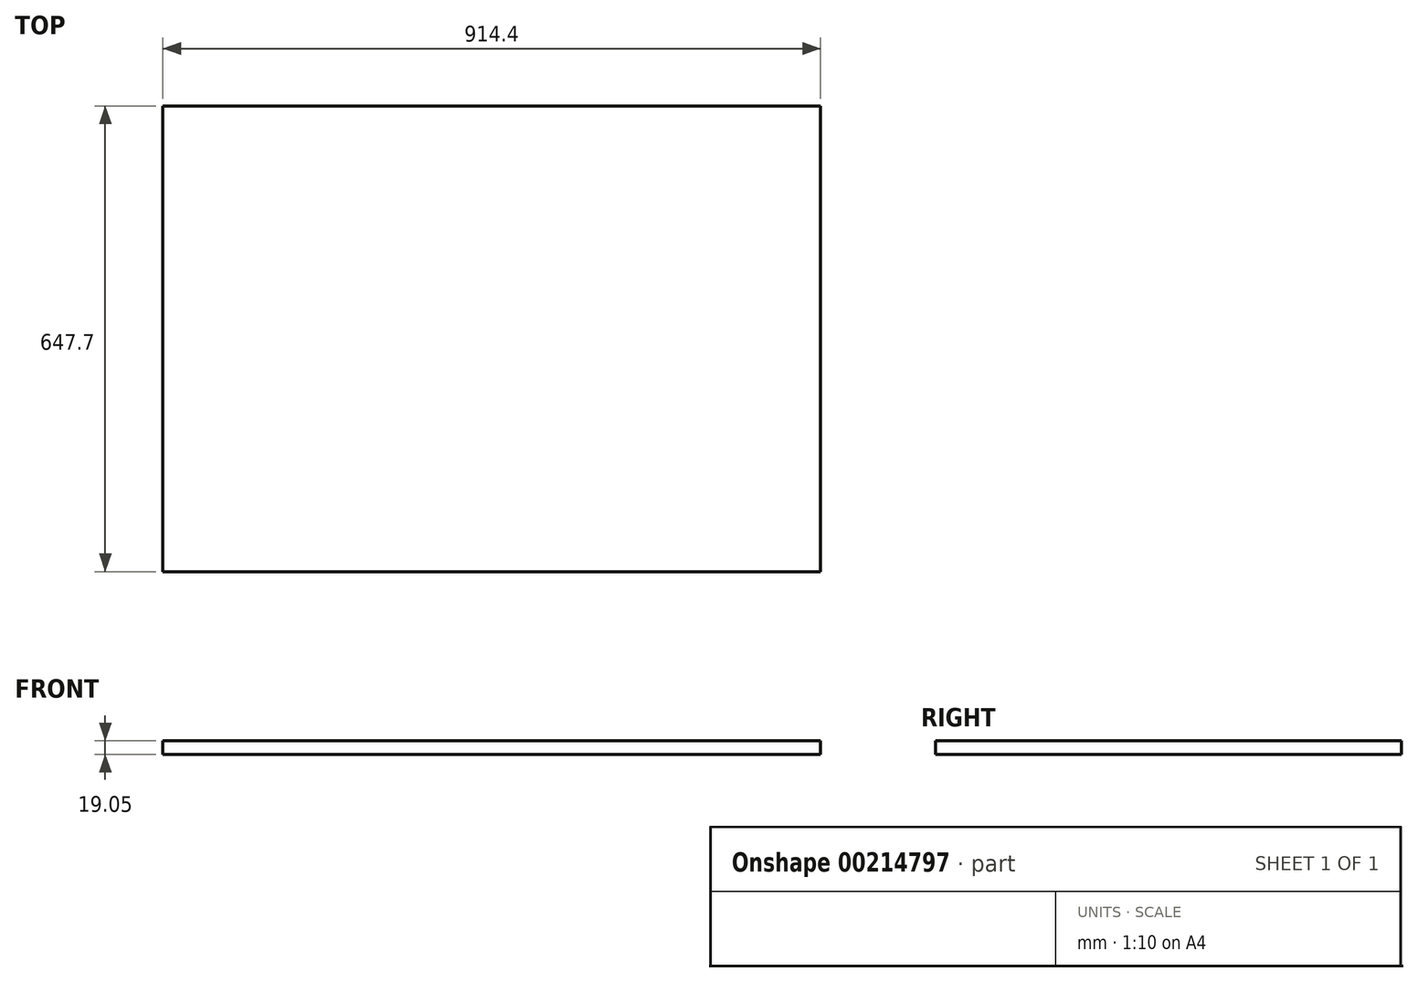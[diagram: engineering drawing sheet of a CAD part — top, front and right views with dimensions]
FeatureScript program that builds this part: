
annotation { "Feature Type Name" : "Feature", "Feature Type Description" : "" }
export const myFeature = defineFeature(function(context is Context, id is Id, definition is map)
    precondition{}
    {
        {
            var Q0;
            Q0=qCreatedBy(makeId("Top.planeOp"),FACE);
            var sketch = newSketch(context, id + "F0", { "sketchPlane" : qUnion([Q0])});
            skLineSegment(sketch, "E0.bottom", {"start": v(0, 0) * mm, "end": v(914.4, 0) * mm});
            skLineSegment(sketch, "E0.top", {"start": v(0, -647.7) * mm, "end": v(914.4, -647.7) * mm});
            skLineSegment(sketch, "E0.left", {"start": v(0, 0) * mm, "end": v(0, -647.7) * mm});
            skLineSegment(sketch, "E0.right", {"start": v(914.4, 0) * mm, "end": v(914.4, -647.7) * mm});
            skSolve(sketch);
        }
        {
            var Q0;
            Q0=makeQuery(id+"F0.imprint","IMPRINT",FACE,{"disambiguationData":[TD([[makeQuery(id+"F0.imprint","IMPRINT",EDGE,{"derivedFrom":sQuery(id+"F0.wireOp",EDGE,"E0.bottom")}),-1.0]])]});
            extrude(context, id + "F1", {"entities" : qUnion([Q0]), "depth" : 19.05 * mm});
        }
    });
